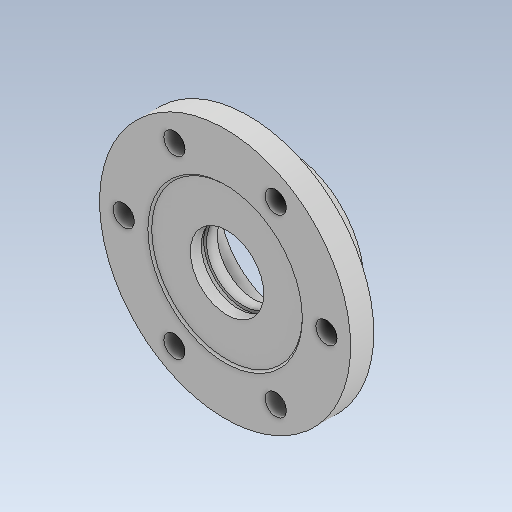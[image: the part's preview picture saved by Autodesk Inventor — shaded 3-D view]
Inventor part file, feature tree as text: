
AUTODESK INVENTOR PART (.ipt)
format: ipt  version: 2020 (Build 240168000, 168)  size: 206,848 bytes
history: native  units: mm
features: extrude x7, sketch x7, plane x3, other x3, reference x2, fillet x1, projected_geometry x1
ambient origin geometry x8: Origin, YZ Plane, XZ Plane, XY Plane, X Axis, Y Axis, Z Axis, Center Point
bodies: 实体1 (feature_tree)
feature tree (24):
  plane  "工作平面1"
  extrude  "拉伸1"  Depth=11.0mm
  extrude  "拉伸2"  Depth=70.0mm
  extrude  "拉伸3"  Depth=12.0mm
  extrude  "拉伸4"  Depth=20.0mm TaperAngle=0.0deg
  fillet  "圆角1"  Radius=30.0mm
  plane  "工作平面2"
  extrude  "拉伸5"  Depth=1.0mm TaperAngle=0.0deg
  extrude  "拉伸6"  Depth=1.0mm
  plane  "工作平面3"
  extrude  "拉伸7"  Depth=2.65mm
  sketch  "草图1"  dims[d0=105.0mm d1=11.0mm]
  reference  "参考1"
  sketch  "草图2"  dims[d2=60.0mm d4=360.0deg d6=70.0mm]
  sketch  "草图3"  dims[d7=12.0mm d8=0.0mm d9=70.0mm]
  reference  "参考2"
  sketch  "草图4"  dims[d10=80.0mm d11=20.0mm d12=0.0mm d14=30.0mm d15=0.0mm]
  sketch  "草图5"  dims[d16=80.0mm d17=1.0mm d18=0.0mm]
  sketch  "草图6"  dims[d19=1.0mm d20=1.0mm]
  projected_geometry  "投影回路1"
  sketch  "草图7"  dims[d21=2.0mm d22=0.0mm d23=38.0mm d24=3.0mm d25=0.0mm d26=-7.0mm d27=40.8mm d28=2.65mm d29=0.0mm]
  other  "<userpath>\Desktop\ME_course_project\课设试试\shaft_try_1.iam"
  other  "shaft_try_1.iam"
  other  "xia(1):1"
